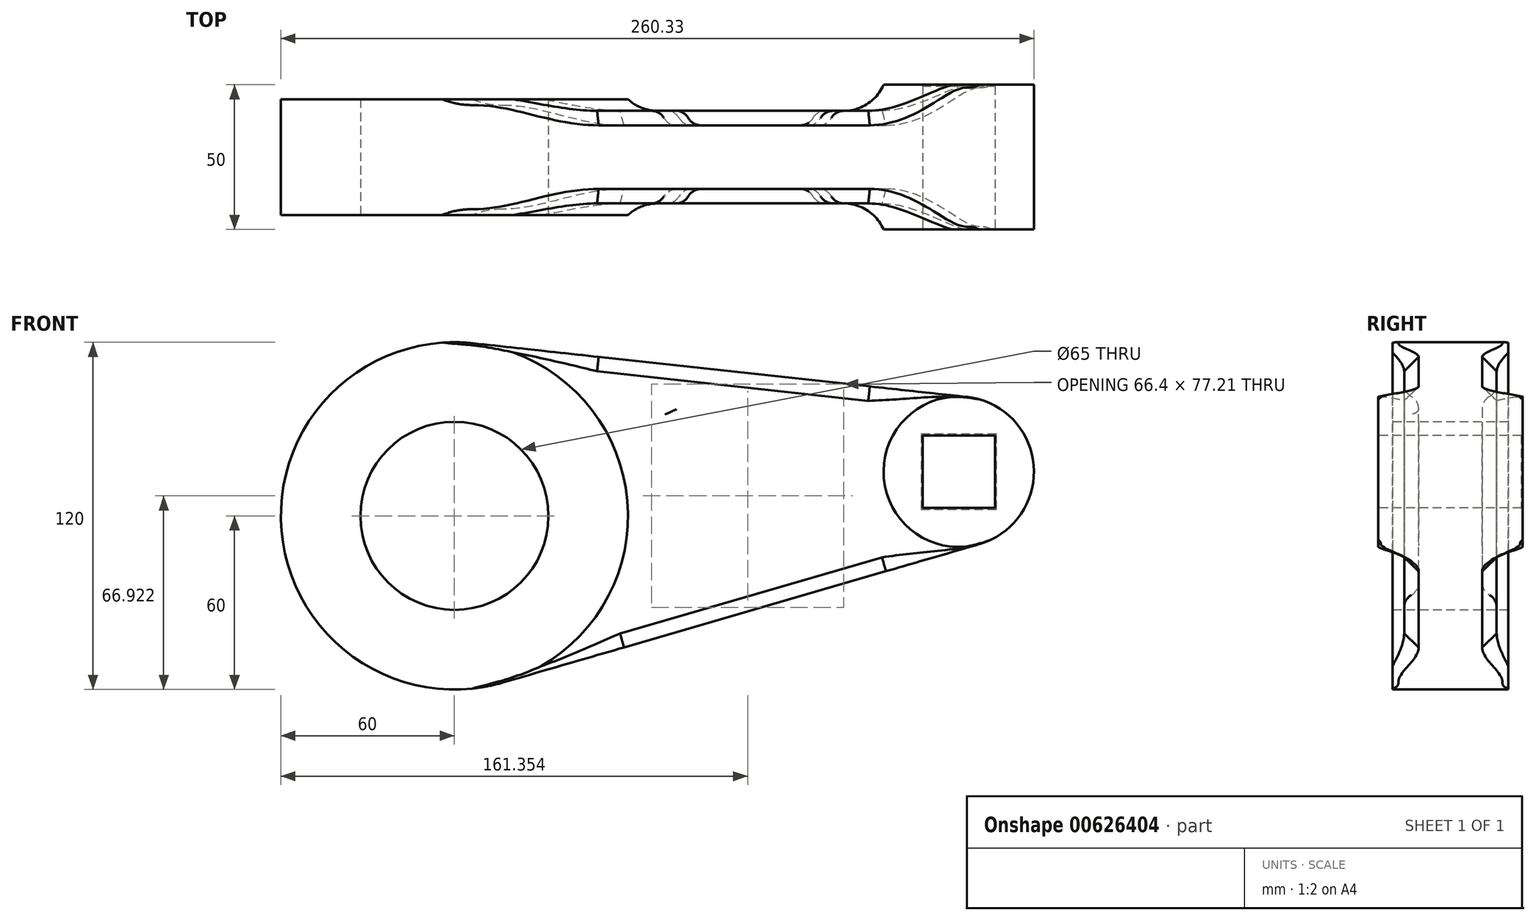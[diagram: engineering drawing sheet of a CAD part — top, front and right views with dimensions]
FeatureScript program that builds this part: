
annotation { "Feature Type Name" : "Feature", "Feature Type Description" : "" }
export const myFeature = defineFeature(function(context is Context, id is Id, definition is map)
    precondition{}
    {
        {
            var Q0;
            Q0=qCreatedBy(makeId("Front.planeOp"),FACE);
            var sketch = newSketch(context, id + "F0", { "sketchPlane" : qUnion([Q0])});
            skCircle(sketch, "E0", {"center": v(0, 0) * mm, "radius": 60 * mm});
            skLineSegment(sketch, "E1", {"start": v(6.48, 59.65) * mm, "end": v(177.14, 41.1) * mm});
            skLineSegment(sketch, "E2", {"start": v(16.74, -57.62) * mm, "end": v(181.59, -9.72) * mm});
            skCircle(sketch, "E3", {"center": v(174.33, 15.25) * mm, "radius": 26 * mm});
            skLineSegment(sketch, "E4", {"start": v(0, 0) * mm, "end": v(174.33, 15.25) * mm});
            skSolve(sketch);
        }
        {
            var Q0;
            {var subQ0=sQuery(id+"F0.wireOp",EDGE,"E0");var subQ1=makeQuery(id+"F0.imprint","INTERSECT",VERTEX,{"derivedFrom":[subQ0,sQuery(id+"F0.wireOp",EDGE,"E1")]});Q0=makeQuery(id+"F0.imprint","IMPRINT",FACE,{"disambiguationData":[TD([[makeQuery(id+"F0.imprint","IMPRINT",EDGE,{"disambiguationData":[TD([[subQ1,1.0]])],"derivedFrom":subQ0}),1.0]])]});}
            var Q1;
            {var subQ0=sQuery(id+"F0.wireOp",EDGE,"E1");Q1=makeQuery(id+"F0.imprint","IMPRINT",FACE,{"disambiguationData":[TD([[makeQuery(id+"F0.imprint","IMPRINT",EDGE,{"derivedFrom":subQ0}),-1.0]])]});}
            var Q2;
            {var subQ0=sQuery(id+"F0.wireOp",EDGE,"E2");Q2=makeQuery(id+"F0.imprint","IMPRINT",FACE,{"disambiguationData":[TD([[makeQuery(id+"F0.imprint","IMPRINT",EDGE,{"derivedFrom":subQ0}),1.0]])]});}
            var Q3;
            {var subQ0=sQuery(id+"F0.wireOp",EDGE,"E3");var subQ1=makeQuery(id+"F0.imprint","INTERSECT",VERTEX,{"derivedFrom":[sQuery(id+"F0.wireOp",EDGE,"E1"),subQ0]});Q3=makeQuery(id+"F0.imprint","IMPRINT",FACE,{"disambiguationData":[TD([[makeQuery(id+"F0.imprint","IMPRINT",EDGE,{"disambiguationData":[TD([[subQ1,-1.0]])],"derivedFrom":subQ0}),1.0]])]});}
            extrude(context, id + "F1", {"entities" : qUnion([Q0, Q1, Q2, Q3]), "endBound" : BoundingType.SYMMETRIC, "depth" : 32 * mm, "offsetDistance" : 25 * mm});
        }
        {
            var Q0;
            {var subQ0=sQuery(id+"F0.wireOp",EDGE,"E0");var subQ1=makeQuery(id+"F0.imprint","INTERSECT",VERTEX,{"derivedFrom":[subQ0,sQuery(id+"F0.wireOp",EDGE,"E1")]});Q0=makeQuery(id+"F0.imprint","IMPRINT",FACE,{"disambiguationData":[TD([[makeQuery(id+"F0.imprint","IMPRINT",EDGE,{"disambiguationData":[TD([[subQ1,1.0]])],"derivedFrom":subQ0}),1.0]])]});}
            extrude(context, id + "F2", {"entities" : qUnion([Q0]), "operationType" : NewBodyOperationType.ADD, "endBound" : BoundingType.SYMMETRIC, "depth" : 40 * mm, "offsetDistance" : 25 * mm});
        }
        {
            var Q0;
            {var subQ0=sQuery(id+"F0.wireOp",EDGE,"E3");var subQ1=makeQuery(id+"F0.imprint","INTERSECT",VERTEX,{"derivedFrom":[sQuery(id+"F0.wireOp",EDGE,"E1"),subQ0]});Q0=makeQuery(id+"F0.imprint","IMPRINT",FACE,{"disambiguationData":[TD([[makeQuery(id+"F0.imprint","IMPRINT",EDGE,{"disambiguationData":[TD([[subQ1,-1.0]])],"derivedFrom":subQ0}),1.0]])]});}
            extrude(context, id + "F3", {"entities" : qUnion([Q0]), "operationType" : NewBodyOperationType.ADD, "endBound" : BoundingType.SYMMETRIC, "depth" : 50 * mm, "offsetDistance" : 25 * mm});
        }
        {
            var Q0;
            Q0=makeQuery(id+"F2.opExtrude","CAP_FACE",FACE,{"disambiguationData":[OSD([sQuery(id+"F0.wireOp",EDGE,"E0")])],"isStart":false});
            var sketch = newSketch(context, id + "F4", { "sketchPlane" : qUnion([Q0])});
            skCircle(sketch, "E5", {"center": v(0, 0) * mm, "radius": 32.5 * mm});
            skSolve(sketch);
        }
        {
            var Q0;
            Q0=makeQuery(id+"F4.imprint","IMPRINT",FACE,{"disambiguationData":[TD([[makeQuery(id+"F4.imprint","IMPRINT",EDGE,{"derivedFrom":sQuery(id+"F4.wireOp",EDGE,"E5")}),1.0]])]});
            extrude(context, id + "F5", {"entities" : qUnion([Q0]), "operationType" : NewBodyOperationType.REMOVE, "endBound" : BoundingType.THROUGH_ALL, "oppositeDirection" : true, "depth" : 25 * mm, "offsetDistance" : 25 * mm});
        }
        {
            var Q0;
            {var subQ0=sQuery(id+"F0.wireOp",EDGE,"E0");Q0=makeQuery(id+"F2.boolean.opBoolean","INTERSECT",EDGE,{"derivedFrom":[makeQuery(id+"F1.opExtrude","CAP_FACE",FACE,{"disambiguationData":[OSD([subQ0,sQuery(id+"F0.wireOp",EDGE,"E1"),sQuery(id+"F0.wireOp",EDGE,"E2"),sQuery(id+"F0.wireOp",EDGE,"E3")])],"isStart":false}),makeQuery(id+"F2.opExtrude","SWEPT_FACE",FACE,{"disambiguationData":[OSD([subQ0])]})]});}
            var Q1;
            {var subQ0=sQuery(id+"F0.wireOp",EDGE,"E0");Q1=makeQuery(id+"F2.boolean.opBoolean","INTERSECT",EDGE,{"derivedFrom":[makeQuery(id+"F1.opExtrude","CAP_FACE",FACE,{"disambiguationData":[OSD([subQ0,sQuery(id+"F0.wireOp",EDGE,"E1"),sQuery(id+"F0.wireOp",EDGE,"E2"),sQuery(id+"F0.wireOp",EDGE,"E3")])],"isStart":true}),makeQuery(id+"F2.opExtrude","SWEPT_FACE",FACE,{"disambiguationData":[OSD([subQ0])]})]});}
            var Q2;
            {var subQ0=sQuery(id+"F0.wireOp",EDGE,"E3");Q2=makeQuery(id+"F3.boolean.opBoolean","INTERSECT",EDGE,{"derivedFrom":[makeQuery(id+"F1.opExtrude","CAP_FACE",FACE,{"disambiguationData":[OSD([sQuery(id+"F0.wireOp",EDGE,"E0"),sQuery(id+"F0.wireOp",EDGE,"E1"),sQuery(id+"F0.wireOp",EDGE,"E2"),subQ0])],"isStart":true}),makeQuery(id+"F3.opExtrude","SWEPT_FACE",FACE,{"disambiguationData":[OSD([subQ0])]})]});}
            var Q3;
            {var subQ0=sQuery(id+"F0.wireOp",EDGE,"E3");Q3=makeQuery(id+"F3.boolean.opBoolean","INTERSECT",EDGE,{"derivedFrom":[makeQuery(id+"F1.opExtrude","CAP_FACE",FACE,{"disambiguationData":[OSD([sQuery(id+"F0.wireOp",EDGE,"E0"),sQuery(id+"F0.wireOp",EDGE,"E1"),sQuery(id+"F0.wireOp",EDGE,"E2"),subQ0])],"isStart":false}),makeQuery(id+"F3.opExtrude","SWEPT_FACE",FACE,{"disambiguationData":[OSD([subQ0])]})]});}
            fillet(context, id + "F6", {"entities" : qUnion([Q0, Q1, Q2, Q3]), "radius" : 15 * mm, "tangentPropagation" : true, "allowEdgeOverflow" : false});
        }
        {
            var Q0;
            Q0=makeQuery(id+"F1.opExtrude","CAP_FACE",FACE,{"disambiguationData":[OSD([sQuery(id+"F0.wireOp",EDGE,"E0"),sQuery(id+"F0.wireOp",EDGE,"E1"),sQuery(id+"F0.wireOp",EDGE,"E2"),sQuery(id+"F0.wireOp",EDGE,"E3")])],"isStart":false});
            var sketch = newSketch(context, id + "F7", { "sketchPlane" : qUnion([Q0])});
            skLineSegment(sketch, "E6.0", {"start": v(74.16, -30.52) * mm, "end": v(133.57, -13.26) * mm});
            skArc(sketch, "E6.1", {"start": v(67.74, 42.93) * mm, "mid": v(79.9, 6.99) * mm, "end": v(74.16, -30.52) * mm});
            skLineSegment(sketch, "E6.2", {"start": v(129.23, 36.25) * mm, "end": v(67.74, 42.93) * mm});
            skArc(sketch, "E6.3", {"start": v(133.57, -13.26) * mm, "mid": v(124.78, 10.92) * mm, "end": v(129.23, 36.25) * mm});
            skSolve(sketch);
        }
        {
            var Q0;
            Q0=makeQuery(id+"F7.imprint","IMPRINT",FACE,{"disambiguationData":[TD([[makeQuery(id+"F7.imprint","IMPRINT",EDGE,{"derivedFrom":sQuery(id+"F7.wireOp",EDGE,"E6.0")}),1.0]])]});
            extrude(context, id + "F8", {"entities" : qUnion([Q0]), "operationType" : NewBodyOperationType.REMOVE, "oppositeDirection" : true, "depth" : 5 * mm, "offsetDistance" : 25 * mm});
        }
        {
            var Q0;
            Q0=makeQuery(id+"F1.opExtrude","CAP_FACE",FACE,{"disambiguationData":[OSD([sQuery(id+"F0.wireOp",EDGE,"E0"),sQuery(id+"F0.wireOp",EDGE,"E1"),sQuery(id+"F0.wireOp",EDGE,"E2"),sQuery(id+"F0.wireOp",EDGE,"E3")])],"isStart":true});
            var sketch = newSketch(context, id + "F9", { "sketchPlane" : qUnion([Q0])});
            skLineSegment(sketch, "E7.0", {"start": v(-67.74, 42.93) * mm, "end": v(-129.23, 36.25) * mm});
            skArc(sketch, "E7.1", {"start": v(-74.16, -30.52) * mm, "mid": v(-79.9, 6.99) * mm, "end": v(-67.74, 42.93) * mm});
            skLineSegment(sketch, "E7.2", {"start": v(-133.57, -13.26) * mm, "end": v(-74.16, -30.52) * mm});
            skArc(sketch, "E7.3", {"start": v(-129.23, 36.25) * mm, "mid": v(-124.78, 10.92) * mm, "end": v(-133.57, -13.26) * mm});
            skSolve(sketch);
        }
        {
            var Q0;
            Q0=makeQuery(id+"F9.imprint","IMPRINT",FACE,{"disambiguationData":[TD([[makeQuery(id+"F9.imprint","IMPRINT",EDGE,{"derivedFrom":sQuery(id+"F9.wireOp",EDGE,"E7.0")}),1.0]])]});
            extrude(context, id + "F10", {"entities" : qUnion([Q0]), "operationType" : NewBodyOperationType.REMOVE, "oppositeDirection" : true, "depth" : 5 * mm, "offsetDistance" : 25 * mm});
        }
        {
            var Q0;
            Q0=makeQuery(id+"F8.boolean.opBoolean","COPY",EDGE,{"derivedFrom":makeQuery(id+"F8.opExtrude","SWEPT_EDGE",EDGE,{"disambiguationData":[OSD([sQuery(id+"F7.wireOp",EDGE,"E6.0"),sQuery(id+"F7.wireOp",EDGE,"E6.1")])]})});
            var Q1;
            Q1=makeQuery(id+"F8.boolean.opBoolean","COPY",EDGE,{"derivedFrom":makeQuery(id+"F8.opExtrude","SWEPT_EDGE",EDGE,{"disambiguationData":[OSD([sQuery(id+"F7.wireOp",EDGE,"E6.1"),sQuery(id+"F7.wireOp",EDGE,"E6.2")])]})});
            var Q2;
            Q2=makeQuery(id+"F8.boolean.opBoolean","COPY",EDGE,{"derivedFrom":makeQuery(id+"F8.opExtrude","SWEPT_EDGE",EDGE,{"disambiguationData":[OSD([sQuery(id+"F7.wireOp",EDGE,"E6.2"),sQuery(id+"F7.wireOp",EDGE,"E6.3")])]})});
            var Q3;
            Q3=makeQuery(id+"F8.boolean.opBoolean","COPY",EDGE,{"derivedFrom":makeQuery(id+"F8.opExtrude","SWEPT_EDGE",EDGE,{"disambiguationData":[OSD([sQuery(id+"F7.wireOp",EDGE,"E6.0"),sQuery(id+"F7.wireOp",EDGE,"E6.3")])]})});
            fillet(context, id + "F11", {"entities" : qUnion([Q0, Q1, Q2, Q3]), "radius" : 5 * mm, "tangentPropagation" : true, "allowEdgeOverflow" : false});
        }
        {
            var Q0;
            Q0=makeQuery(id+"F10.boolean.opBoolean","COPY",EDGE,{"derivedFrom":makeQuery(id+"F10.opExtrude","SWEPT_EDGE",EDGE,{"disambiguationData":[OSD([sQuery(id+"F9.wireOp",EDGE,"E7.2"),sQuery(id+"F9.wireOp",EDGE,"E7.3")])]})});
            var Q1;
            Q1=makeQuery(id+"F10.boolean.opBoolean","COPY",EDGE,{"derivedFrom":makeQuery(id+"F10.opExtrude","SWEPT_EDGE",EDGE,{"disambiguationData":[OSD([sQuery(id+"F9.wireOp",EDGE,"E7.0"),sQuery(id+"F9.wireOp",EDGE,"E7.3")])]})});
            var Q2;
            Q2=makeQuery(id+"F10.boolean.opBoolean","COPY",EDGE,{"derivedFrom":makeQuery(id+"F10.opExtrude","SWEPT_EDGE",EDGE,{"disambiguationData":[OSD([sQuery(id+"F9.wireOp",EDGE,"E7.0"),sQuery(id+"F9.wireOp",EDGE,"E7.1")])]})});
            var Q3;
            Q3=makeQuery(id+"F10.boolean.opBoolean","COPY",EDGE,{"derivedFrom":makeQuery(id+"F10.opExtrude","SWEPT_EDGE",EDGE,{"disambiguationData":[OSD([sQuery(id+"F9.wireOp",EDGE,"E7.1"),sQuery(id+"F9.wireOp",EDGE,"E7.2")])]})});
            fillet(context, id + "F12", {"entities" : qUnion([Q0, Q1, Q2, Q3]), "radius" : 5 * mm, "tangentPropagation" : true, "allowEdgeOverflow" : false});
        }
        {
            var Q0;
            Q0=makeQuery(id+"F10.boolean.opBoolean","COPY",FACE,{"derivedFrom":makeQuery(id+"F10.opExtrude","CAP_FACE",FACE,{"disambiguationData":[OSD([sQuery(id+"F9.wireOp",EDGE,"E7.0"),sQuery(id+"F9.wireOp",EDGE,"E7.1"),sQuery(id+"F9.wireOp",EDGE,"E7.2"),sQuery(id+"F9.wireOp",EDGE,"E7.3")])],"isStart":false})});
            fillet(context, id + "F13", {"entities" : qUnion([Q0]), "radius" : 5 * mm, "tangentPropagation" : true, "allowEdgeOverflow" : false});
        }
        {
            var Q0;
            Q0=makeQuery(id+"F8.boolean.opBoolean","COPY",FACE,{"derivedFrom":makeQuery(id+"F8.opExtrude","CAP_FACE",FACE,{"disambiguationData":[OSD([sQuery(id+"F7.wireOp",EDGE,"E6.0"),sQuery(id+"F7.wireOp",EDGE,"E6.1"),sQuery(id+"F7.wireOp",EDGE,"E6.2"),sQuery(id+"F7.wireOp",EDGE,"E6.3")])],"isStart":false})});
            fillet(context, id + "F14", {"entities" : qUnion([Q0]), "radius" : 5 * mm, "tangentPropagation" : true, "allowEdgeOverflow" : false});
        }
        {
            var Q0;
            Q0=makeQuery(id+"F14.opFillet","BLEND_EDGE",EDGE,{"blendedFrom":[makeQuery(id+"F8.boolean.opBoolean","COPY",EDGE,{"derivedFrom":makeQuery(id+"F8.opExtrude","CAP_EDGE",EDGE,{"disambiguationData":[OSD([sQuery(id+"F7.wireOp",EDGE,"E6.2")])],"isStart":false})}),makeQuery(id+"F1.opExtrude","CAP_FACE",FACE,{"disambiguationData":[OSD([sQuery(id+"F0.wireOp",EDGE,"E0"),sQuery(id+"F0.wireOp",EDGE,"E1"),sQuery(id+"F0.wireOp",EDGE,"E2"),sQuery(id+"F0.wireOp",EDGE,"E3")])],"isStart":false})],"blendedInto":[makeQuery(id+"F1.opExtrude","CAP_FACE",FACE,{"disambiguationData":[OSD([sQuery(id+"F0.wireOp",EDGE,"E0"),sQuery(id+"F0.wireOp",EDGE,"E1"),sQuery(id+"F0.wireOp",EDGE,"E2"),sQuery(id+"F0.wireOp",EDGE,"E3")])],"isStart":false})]});
            var Q1;
            {var subQ0=sQuery(id+"F7.wireOp",EDGE,"E6.2");var subQ1=sQuery(id+"F7.wireOp",EDGE,"E6.1");Q1=makeQuery(id+"F14.opFillet","BLEND_EDGE",EDGE,{"blendedFrom":[makeQuery(id+"F11.opFillet","BLEND_EDGE",EDGE,{"blendedFrom":[makeQuery(id+"F8.boolean.opBoolean","COPY",EDGE,{"derivedFrom":makeQuery(id+"F8.opExtrude","SWEPT_EDGE",EDGE,{"disambiguationData":[OSD([subQ1,subQ0])]})}),makeQuery(id+"F8.boolean.opBoolean","COPY",FACE,{"derivedFrom":makeQuery(id+"F8.opExtrude","CAP_FACE",FACE,{"disambiguationData":[OSD([sQuery(id+"F7.wireOp",EDGE,"E6.0"),subQ1,subQ0,sQuery(id+"F7.wireOp",EDGE,"E6.3")])],"isStart":false})})],"blendedInto":[makeQuery(id+"F8.boolean.opBoolean","COPY",FACE,{"derivedFrom":makeQuery(id+"F8.opExtrude","CAP_FACE",FACE,{"disambiguationData":[OSD([sQuery(id+"F7.wireOp",EDGE,"E6.0"),subQ1,subQ0,sQuery(id+"F7.wireOp",EDGE,"E6.3")])],"isStart":false})})]}),makeQuery(id+"F1.opExtrude","CAP_FACE",FACE,{"disambiguationData":[OSD([sQuery(id+"F0.wireOp",EDGE,"E0"),sQuery(id+"F0.wireOp",EDGE,"E1"),sQuery(id+"F0.wireOp",EDGE,"E2"),sQuery(id+"F0.wireOp",EDGE,"E3")])],"isStart":false})],"blendedInto":[makeQuery(id+"F1.opExtrude","CAP_FACE",FACE,{"disambiguationData":[OSD([sQuery(id+"F0.wireOp",EDGE,"E0"),sQuery(id+"F0.wireOp",EDGE,"E1"),sQuery(id+"F0.wireOp",EDGE,"E2"),sQuery(id+"F0.wireOp",EDGE,"E3")])],"isStart":false})]});}
            var Q2;
            Q2=makeQuery(id+"F14.opFillet","BLEND_EDGE",EDGE,{"blendedFrom":[makeQuery(id+"F8.boolean.opBoolean","COPY",EDGE,{"derivedFrom":makeQuery(id+"F8.opExtrude","CAP_EDGE",EDGE,{"disambiguationData":[OSD([sQuery(id+"F7.wireOp",EDGE,"E6.1")])],"isStart":false})}),makeQuery(id+"F1.opExtrude","CAP_FACE",FACE,{"disambiguationData":[OSD([sQuery(id+"F0.wireOp",EDGE,"E0"),sQuery(id+"F0.wireOp",EDGE,"E1"),sQuery(id+"F0.wireOp",EDGE,"E2"),sQuery(id+"F0.wireOp",EDGE,"E3")])],"isStart":false})],"blendedInto":[makeQuery(id+"F1.opExtrude","CAP_FACE",FACE,{"disambiguationData":[OSD([sQuery(id+"F0.wireOp",EDGE,"E0"),sQuery(id+"F0.wireOp",EDGE,"E1"),sQuery(id+"F0.wireOp",EDGE,"E2"),sQuery(id+"F0.wireOp",EDGE,"E3")])],"isStart":false})]});
            var Q3;
            {var subQ0=sQuery(id+"F7.wireOp",EDGE,"E6.1");var subQ1=sQuery(id+"F7.wireOp",EDGE,"E6.0");Q3=makeQuery(id+"F14.opFillet","BLEND_EDGE",EDGE,{"blendedFrom":[makeQuery(id+"F11.opFillet","BLEND_EDGE",EDGE,{"blendedFrom":[makeQuery(id+"F8.boolean.opBoolean","COPY",EDGE,{"derivedFrom":makeQuery(id+"F8.opExtrude","SWEPT_EDGE",EDGE,{"disambiguationData":[OSD([subQ1,subQ0])]})}),makeQuery(id+"F8.boolean.opBoolean","COPY",FACE,{"derivedFrom":makeQuery(id+"F8.opExtrude","CAP_FACE",FACE,{"disambiguationData":[OSD([subQ1,subQ0,sQuery(id+"F7.wireOp",EDGE,"E6.2"),sQuery(id+"F7.wireOp",EDGE,"E6.3")])],"isStart":false})})],"blendedInto":[makeQuery(id+"F8.boolean.opBoolean","COPY",FACE,{"derivedFrom":makeQuery(id+"F8.opExtrude","CAP_FACE",FACE,{"disambiguationData":[OSD([subQ1,subQ0,sQuery(id+"F7.wireOp",EDGE,"E6.2"),sQuery(id+"F7.wireOp",EDGE,"E6.3")])],"isStart":false})})]}),makeQuery(id+"F1.opExtrude","CAP_FACE",FACE,{"disambiguationData":[OSD([sQuery(id+"F0.wireOp",EDGE,"E0"),sQuery(id+"F0.wireOp",EDGE,"E1"),sQuery(id+"F0.wireOp",EDGE,"E2"),sQuery(id+"F0.wireOp",EDGE,"E3")])],"isStart":false})],"blendedInto":[makeQuery(id+"F1.opExtrude","CAP_FACE",FACE,{"disambiguationData":[OSD([sQuery(id+"F0.wireOp",EDGE,"E0"),sQuery(id+"F0.wireOp",EDGE,"E1"),sQuery(id+"F0.wireOp",EDGE,"E2"),sQuery(id+"F0.wireOp",EDGE,"E3")])],"isStart":false})]});}
            var Q4;
            Q4=makeQuery(id+"F14.opFillet","BLEND_EDGE",EDGE,{"blendedFrom":[makeQuery(id+"F8.boolean.opBoolean","COPY",EDGE,{"derivedFrom":makeQuery(id+"F8.opExtrude","CAP_EDGE",EDGE,{"disambiguationData":[OSD([sQuery(id+"F7.wireOp",EDGE,"E6.0")])],"isStart":false})}),makeQuery(id+"F1.opExtrude","CAP_FACE",FACE,{"disambiguationData":[OSD([sQuery(id+"F0.wireOp",EDGE,"E0"),sQuery(id+"F0.wireOp",EDGE,"E1"),sQuery(id+"F0.wireOp",EDGE,"E2"),sQuery(id+"F0.wireOp",EDGE,"E3")])],"isStart":false})],"blendedInto":[makeQuery(id+"F1.opExtrude","CAP_FACE",FACE,{"disambiguationData":[OSD([sQuery(id+"F0.wireOp",EDGE,"E0"),sQuery(id+"F0.wireOp",EDGE,"E1"),sQuery(id+"F0.wireOp",EDGE,"E2"),sQuery(id+"F0.wireOp",EDGE,"E3")])],"isStart":false})]});
            var Q5;
            {var subQ0=sQuery(id+"F7.wireOp",EDGE,"E6.3");var subQ1=sQuery(id+"F7.wireOp",EDGE,"E6.0");Q5=makeQuery(id+"F14.opFillet","BLEND_EDGE",EDGE,{"blendedFrom":[makeQuery(id+"F11.opFillet","BLEND_EDGE",EDGE,{"blendedFrom":[makeQuery(id+"F8.boolean.opBoolean","COPY",EDGE,{"derivedFrom":makeQuery(id+"F8.opExtrude","SWEPT_EDGE",EDGE,{"disambiguationData":[OSD([subQ1,subQ0])]})}),makeQuery(id+"F8.boolean.opBoolean","COPY",FACE,{"derivedFrom":makeQuery(id+"F8.opExtrude","CAP_FACE",FACE,{"disambiguationData":[OSD([subQ1,sQuery(id+"F7.wireOp",EDGE,"E6.1"),sQuery(id+"F7.wireOp",EDGE,"E6.2"),subQ0])],"isStart":false})})],"blendedInto":[makeQuery(id+"F8.boolean.opBoolean","COPY",FACE,{"derivedFrom":makeQuery(id+"F8.opExtrude","CAP_FACE",FACE,{"disambiguationData":[OSD([subQ1,sQuery(id+"F7.wireOp",EDGE,"E6.1"),sQuery(id+"F7.wireOp",EDGE,"E6.2"),subQ0])],"isStart":false})})]}),makeQuery(id+"F1.opExtrude","CAP_FACE",FACE,{"disambiguationData":[OSD([sQuery(id+"F0.wireOp",EDGE,"E0"),sQuery(id+"F0.wireOp",EDGE,"E1"),sQuery(id+"F0.wireOp",EDGE,"E2"),sQuery(id+"F0.wireOp",EDGE,"E3")])],"isStart":false})],"blendedInto":[makeQuery(id+"F1.opExtrude","CAP_FACE",FACE,{"disambiguationData":[OSD([sQuery(id+"F0.wireOp",EDGE,"E0"),sQuery(id+"F0.wireOp",EDGE,"E1"),sQuery(id+"F0.wireOp",EDGE,"E2"),sQuery(id+"F0.wireOp",EDGE,"E3")])],"isStart":false})]});}
            var Q6;
            Q6=makeQuery(id+"F14.opFillet","BLEND_EDGE",EDGE,{"blendedFrom":[makeQuery(id+"F8.boolean.opBoolean","COPY",EDGE,{"derivedFrom":makeQuery(id+"F8.opExtrude","CAP_EDGE",EDGE,{"disambiguationData":[OSD([sQuery(id+"F7.wireOp",EDGE,"E6.3")])],"isStart":false})}),makeQuery(id+"F1.opExtrude","CAP_FACE",FACE,{"disambiguationData":[OSD([sQuery(id+"F0.wireOp",EDGE,"E0"),sQuery(id+"F0.wireOp",EDGE,"E1"),sQuery(id+"F0.wireOp",EDGE,"E2"),sQuery(id+"F0.wireOp",EDGE,"E3")])],"isStart":false})],"blendedInto":[makeQuery(id+"F1.opExtrude","CAP_FACE",FACE,{"disambiguationData":[OSD([sQuery(id+"F0.wireOp",EDGE,"E0"),sQuery(id+"F0.wireOp",EDGE,"E1"),sQuery(id+"F0.wireOp",EDGE,"E2"),sQuery(id+"F0.wireOp",EDGE,"E3")])],"isStart":false})]});
            var Q7;
            {var subQ0=sQuery(id+"F7.wireOp",EDGE,"E6.3");var subQ1=sQuery(id+"F7.wireOp",EDGE,"E6.2");Q7=makeQuery(id+"F14.opFillet","BLEND_EDGE",EDGE,{"blendedFrom":[makeQuery(id+"F11.opFillet","BLEND_EDGE",EDGE,{"blendedFrom":[makeQuery(id+"F8.boolean.opBoolean","COPY",EDGE,{"derivedFrom":makeQuery(id+"F8.opExtrude","SWEPT_EDGE",EDGE,{"disambiguationData":[OSD([subQ1,subQ0])]})}),makeQuery(id+"F8.boolean.opBoolean","COPY",FACE,{"derivedFrom":makeQuery(id+"F8.opExtrude","CAP_FACE",FACE,{"disambiguationData":[OSD([sQuery(id+"F7.wireOp",EDGE,"E6.0"),sQuery(id+"F7.wireOp",EDGE,"E6.1"),subQ1,subQ0])],"isStart":false})})],"blendedInto":[makeQuery(id+"F8.boolean.opBoolean","COPY",FACE,{"derivedFrom":makeQuery(id+"F8.opExtrude","CAP_FACE",FACE,{"disambiguationData":[OSD([sQuery(id+"F7.wireOp",EDGE,"E6.0"),sQuery(id+"F7.wireOp",EDGE,"E6.1"),subQ1,subQ0])],"isStart":false})})]}),makeQuery(id+"F1.opExtrude","CAP_FACE",FACE,{"disambiguationData":[OSD([sQuery(id+"F0.wireOp",EDGE,"E0"),sQuery(id+"F0.wireOp",EDGE,"E1"),sQuery(id+"F0.wireOp",EDGE,"E2"),sQuery(id+"F0.wireOp",EDGE,"E3")])],"isStart":false})],"blendedInto":[makeQuery(id+"F1.opExtrude","CAP_FACE",FACE,{"disambiguationData":[OSD([sQuery(id+"F0.wireOp",EDGE,"E0"),sQuery(id+"F0.wireOp",EDGE,"E1"),sQuery(id+"F0.wireOp",EDGE,"E2"),sQuery(id+"F0.wireOp",EDGE,"E3")])],"isStart":false})]});}
            fillet(context, id + "F15", {"entities" : qUnion([Q0, Q1, Q2, Q3, Q4, Q5, Q6, Q7]), "radius" : 5 * mm, "tangentPropagation" : true, "allowEdgeOverflow" : false});
        }
        {
            var Q0;
            Q0=makeQuery(id+"F13.opFillet","BLEND_EDGE",EDGE,{"blendedFrom":[makeQuery(id+"F10.boolean.opBoolean","COPY",EDGE,{"derivedFrom":makeQuery(id+"F10.opExtrude","CAP_EDGE",EDGE,{"disambiguationData":[OSD([sQuery(id+"F9.wireOp",EDGE,"E7.0")])],"isStart":false})}),makeQuery(id+"F1.opExtrude","CAP_FACE",FACE,{"disambiguationData":[OSD([sQuery(id+"F0.wireOp",EDGE,"E0"),sQuery(id+"F0.wireOp",EDGE,"E1"),sQuery(id+"F0.wireOp",EDGE,"E2"),sQuery(id+"F0.wireOp",EDGE,"E3")])],"isStart":true})],"blendedInto":[makeQuery(id+"F1.opExtrude","CAP_FACE",FACE,{"disambiguationData":[OSD([sQuery(id+"F0.wireOp",EDGE,"E0"),sQuery(id+"F0.wireOp",EDGE,"E1"),sQuery(id+"F0.wireOp",EDGE,"E2"),sQuery(id+"F0.wireOp",EDGE,"E3")])],"isStart":true})]});
            var Q1;
            {var subQ0=sQuery(id+"F9.wireOp",EDGE,"E7.1");var subQ1=sQuery(id+"F9.wireOp",EDGE,"E7.0");Q1=makeQuery(id+"F13.opFillet","BLEND_EDGE",EDGE,{"blendedFrom":[makeQuery(id+"F12.opFillet","BLEND_EDGE",EDGE,{"blendedFrom":[makeQuery(id+"F10.boolean.opBoolean","COPY",EDGE,{"derivedFrom":makeQuery(id+"F10.opExtrude","SWEPT_EDGE",EDGE,{"disambiguationData":[OSD([subQ1,subQ0])]})}),makeQuery(id+"F10.boolean.opBoolean","COPY",FACE,{"derivedFrom":makeQuery(id+"F10.opExtrude","CAP_FACE",FACE,{"disambiguationData":[OSD([subQ1,subQ0,sQuery(id+"F9.wireOp",EDGE,"E7.2"),sQuery(id+"F9.wireOp",EDGE,"E7.3")])],"isStart":false})})],"blendedInto":[makeQuery(id+"F10.boolean.opBoolean","COPY",FACE,{"derivedFrom":makeQuery(id+"F10.opExtrude","CAP_FACE",FACE,{"disambiguationData":[OSD([subQ1,subQ0,sQuery(id+"F9.wireOp",EDGE,"E7.2"),sQuery(id+"F9.wireOp",EDGE,"E7.3")])],"isStart":false})})]}),makeQuery(id+"F1.opExtrude","CAP_FACE",FACE,{"disambiguationData":[OSD([sQuery(id+"F0.wireOp",EDGE,"E0"),sQuery(id+"F0.wireOp",EDGE,"E1"),sQuery(id+"F0.wireOp",EDGE,"E2"),sQuery(id+"F0.wireOp",EDGE,"E3")])],"isStart":true})],"blendedInto":[makeQuery(id+"F1.opExtrude","CAP_FACE",FACE,{"disambiguationData":[OSD([sQuery(id+"F0.wireOp",EDGE,"E0"),sQuery(id+"F0.wireOp",EDGE,"E1"),sQuery(id+"F0.wireOp",EDGE,"E2"),sQuery(id+"F0.wireOp",EDGE,"E3")])],"isStart":true})]});}
            var Q2;
            Q2=makeQuery(id+"F13.opFillet","BLEND_EDGE",EDGE,{"blendedFrom":[makeQuery(id+"F10.boolean.opBoolean","COPY",EDGE,{"derivedFrom":makeQuery(id+"F10.opExtrude","CAP_EDGE",EDGE,{"disambiguationData":[OSD([sQuery(id+"F9.wireOp",EDGE,"E7.1")])],"isStart":false})}),makeQuery(id+"F1.opExtrude","CAP_FACE",FACE,{"disambiguationData":[OSD([sQuery(id+"F0.wireOp",EDGE,"E0"),sQuery(id+"F0.wireOp",EDGE,"E1"),sQuery(id+"F0.wireOp",EDGE,"E2"),sQuery(id+"F0.wireOp",EDGE,"E3")])],"isStart":true})],"blendedInto":[makeQuery(id+"F1.opExtrude","CAP_FACE",FACE,{"disambiguationData":[OSD([sQuery(id+"F0.wireOp",EDGE,"E0"),sQuery(id+"F0.wireOp",EDGE,"E1"),sQuery(id+"F0.wireOp",EDGE,"E2"),sQuery(id+"F0.wireOp",EDGE,"E3")])],"isStart":true})]});
            var Q3;
            {var subQ0=sQuery(id+"F9.wireOp",EDGE,"E7.2");var subQ1=sQuery(id+"F9.wireOp",EDGE,"E7.1");Q3=makeQuery(id+"F13.opFillet","BLEND_EDGE",EDGE,{"blendedFrom":[makeQuery(id+"F12.opFillet","BLEND_EDGE",EDGE,{"blendedFrom":[makeQuery(id+"F10.boolean.opBoolean","COPY",EDGE,{"derivedFrom":makeQuery(id+"F10.opExtrude","SWEPT_EDGE",EDGE,{"disambiguationData":[OSD([subQ1,subQ0])]})}),makeQuery(id+"F10.boolean.opBoolean","COPY",FACE,{"derivedFrom":makeQuery(id+"F10.opExtrude","CAP_FACE",FACE,{"disambiguationData":[OSD([sQuery(id+"F9.wireOp",EDGE,"E7.0"),subQ1,subQ0,sQuery(id+"F9.wireOp",EDGE,"E7.3")])],"isStart":false})})],"blendedInto":[makeQuery(id+"F10.boolean.opBoolean","COPY",FACE,{"derivedFrom":makeQuery(id+"F10.opExtrude","CAP_FACE",FACE,{"disambiguationData":[OSD([sQuery(id+"F9.wireOp",EDGE,"E7.0"),subQ1,subQ0,sQuery(id+"F9.wireOp",EDGE,"E7.3")])],"isStart":false})})]}),makeQuery(id+"F1.opExtrude","CAP_FACE",FACE,{"disambiguationData":[OSD([sQuery(id+"F0.wireOp",EDGE,"E0"),sQuery(id+"F0.wireOp",EDGE,"E1"),sQuery(id+"F0.wireOp",EDGE,"E2"),sQuery(id+"F0.wireOp",EDGE,"E3")])],"isStart":true})],"blendedInto":[makeQuery(id+"F1.opExtrude","CAP_FACE",FACE,{"disambiguationData":[OSD([sQuery(id+"F0.wireOp",EDGE,"E0"),sQuery(id+"F0.wireOp",EDGE,"E1"),sQuery(id+"F0.wireOp",EDGE,"E2"),sQuery(id+"F0.wireOp",EDGE,"E3")])],"isStart":true})]});}
            var Q4;
            Q4=makeQuery(id+"F13.opFillet","BLEND_EDGE",EDGE,{"blendedFrom":[makeQuery(id+"F10.boolean.opBoolean","COPY",EDGE,{"derivedFrom":makeQuery(id+"F10.opExtrude","CAP_EDGE",EDGE,{"disambiguationData":[OSD([sQuery(id+"F9.wireOp",EDGE,"E7.2")])],"isStart":false})}),makeQuery(id+"F1.opExtrude","CAP_FACE",FACE,{"disambiguationData":[OSD([sQuery(id+"F0.wireOp",EDGE,"E0"),sQuery(id+"F0.wireOp",EDGE,"E1"),sQuery(id+"F0.wireOp",EDGE,"E2"),sQuery(id+"F0.wireOp",EDGE,"E3")])],"isStart":true})],"blendedInto":[makeQuery(id+"F1.opExtrude","CAP_FACE",FACE,{"disambiguationData":[OSD([sQuery(id+"F0.wireOp",EDGE,"E0"),sQuery(id+"F0.wireOp",EDGE,"E1"),sQuery(id+"F0.wireOp",EDGE,"E2"),sQuery(id+"F0.wireOp",EDGE,"E3")])],"isStart":true})]});
            var Q5;
            {var subQ0=sQuery(id+"F9.wireOp",EDGE,"E7.3");var subQ1=sQuery(id+"F9.wireOp",EDGE,"E7.2");Q5=makeQuery(id+"F13.opFillet","BLEND_EDGE",EDGE,{"blendedFrom":[makeQuery(id+"F12.opFillet","BLEND_EDGE",EDGE,{"blendedFrom":[makeQuery(id+"F10.boolean.opBoolean","COPY",EDGE,{"derivedFrom":makeQuery(id+"F10.opExtrude","SWEPT_EDGE",EDGE,{"disambiguationData":[OSD([subQ1,subQ0])]})}),makeQuery(id+"F10.boolean.opBoolean","COPY",FACE,{"derivedFrom":makeQuery(id+"F10.opExtrude","CAP_FACE",FACE,{"disambiguationData":[OSD([sQuery(id+"F9.wireOp",EDGE,"E7.0"),sQuery(id+"F9.wireOp",EDGE,"E7.1"),subQ1,subQ0])],"isStart":false})})],"blendedInto":[makeQuery(id+"F10.boolean.opBoolean","COPY",FACE,{"derivedFrom":makeQuery(id+"F10.opExtrude","CAP_FACE",FACE,{"disambiguationData":[OSD([sQuery(id+"F9.wireOp",EDGE,"E7.0"),sQuery(id+"F9.wireOp",EDGE,"E7.1"),subQ1,subQ0])],"isStart":false})})]}),makeQuery(id+"F1.opExtrude","CAP_FACE",FACE,{"disambiguationData":[OSD([sQuery(id+"F0.wireOp",EDGE,"E0"),sQuery(id+"F0.wireOp",EDGE,"E1"),sQuery(id+"F0.wireOp",EDGE,"E2"),sQuery(id+"F0.wireOp",EDGE,"E3")])],"isStart":true})],"blendedInto":[makeQuery(id+"F1.opExtrude","CAP_FACE",FACE,{"disambiguationData":[OSD([sQuery(id+"F0.wireOp",EDGE,"E0"),sQuery(id+"F0.wireOp",EDGE,"E1"),sQuery(id+"F0.wireOp",EDGE,"E2"),sQuery(id+"F0.wireOp",EDGE,"E3")])],"isStart":true})]});}
            var Q6;
            Q6=makeQuery(id+"F13.opFillet","BLEND_EDGE",EDGE,{"blendedFrom":[makeQuery(id+"F10.boolean.opBoolean","COPY",EDGE,{"derivedFrom":makeQuery(id+"F10.opExtrude","CAP_EDGE",EDGE,{"disambiguationData":[OSD([sQuery(id+"F9.wireOp",EDGE,"E7.3")])],"isStart":false})}),makeQuery(id+"F1.opExtrude","CAP_FACE",FACE,{"disambiguationData":[OSD([sQuery(id+"F0.wireOp",EDGE,"E0"),sQuery(id+"F0.wireOp",EDGE,"E1"),sQuery(id+"F0.wireOp",EDGE,"E2"),sQuery(id+"F0.wireOp",EDGE,"E3")])],"isStart":true})],"blendedInto":[makeQuery(id+"F1.opExtrude","CAP_FACE",FACE,{"disambiguationData":[OSD([sQuery(id+"F0.wireOp",EDGE,"E0"),sQuery(id+"F0.wireOp",EDGE,"E1"),sQuery(id+"F0.wireOp",EDGE,"E2"),sQuery(id+"F0.wireOp",EDGE,"E3")])],"isStart":true})]});
            var Q7;
            {var subQ0=sQuery(id+"F9.wireOp",EDGE,"E7.3");var subQ1=sQuery(id+"F9.wireOp",EDGE,"E7.0");Q7=makeQuery(id+"F13.opFillet","BLEND_EDGE",EDGE,{"blendedFrom":[makeQuery(id+"F12.opFillet","BLEND_EDGE",EDGE,{"blendedFrom":[makeQuery(id+"F10.boolean.opBoolean","COPY",EDGE,{"derivedFrom":makeQuery(id+"F10.opExtrude","SWEPT_EDGE",EDGE,{"disambiguationData":[OSD([subQ1,subQ0])]})}),makeQuery(id+"F10.boolean.opBoolean","COPY",FACE,{"derivedFrom":makeQuery(id+"F10.opExtrude","CAP_FACE",FACE,{"disambiguationData":[OSD([subQ1,sQuery(id+"F9.wireOp",EDGE,"E7.1"),sQuery(id+"F9.wireOp",EDGE,"E7.2"),subQ0])],"isStart":false})})],"blendedInto":[makeQuery(id+"F10.boolean.opBoolean","COPY",FACE,{"derivedFrom":makeQuery(id+"F10.opExtrude","CAP_FACE",FACE,{"disambiguationData":[OSD([subQ1,sQuery(id+"F9.wireOp",EDGE,"E7.1"),sQuery(id+"F9.wireOp",EDGE,"E7.2"),subQ0])],"isStart":false})})]}),makeQuery(id+"F1.opExtrude","CAP_FACE",FACE,{"disambiguationData":[OSD([sQuery(id+"F0.wireOp",EDGE,"E0"),sQuery(id+"F0.wireOp",EDGE,"E1"),sQuery(id+"F0.wireOp",EDGE,"E2"),sQuery(id+"F0.wireOp",EDGE,"E3")])],"isStart":true})],"blendedInto":[makeQuery(id+"F1.opExtrude","CAP_FACE",FACE,{"disambiguationData":[OSD([sQuery(id+"F0.wireOp",EDGE,"E0"),sQuery(id+"F0.wireOp",EDGE,"E1"),sQuery(id+"F0.wireOp",EDGE,"E2"),sQuery(id+"F0.wireOp",EDGE,"E3")])],"isStart":true})]});}
            fillet(context, id + "F16", {"entities" : qUnion([Q0, Q1, Q2, Q3, Q4, Q5, Q6, Q7]), "radius" : 5 * mm, "tangentPropagation" : true, "allowEdgeOverflow" : false});
        }
        {
            var Q0;
            Q0=makeQuery(id+"F1.opExtrude","CAP_EDGE",EDGE,{"disambiguationData":[OSD([sQuery(id+"F0.wireOp",EDGE,"E1")])],"isStart":true});
            var Q1;
            Q1=makeQuery(id+"F1.opExtrude","CAP_EDGE",EDGE,{"disambiguationData":[OSD([sQuery(id+"F0.wireOp",EDGE,"E2")])],"isStart":true});
            var Q2;
            Q2=makeQuery(id+"F1.opExtrude","CAP_EDGE",EDGE,{"disambiguationData":[OSD([sQuery(id+"F0.wireOp",EDGE,"E1")])],"isStart":false});
            var Q3;
            Q3=makeQuery(id+"F1.opExtrude","CAP_EDGE",EDGE,{"disambiguationData":[OSD([sQuery(id+"F0.wireOp",EDGE,"E2")])],"isStart":false});
            chamfer(context, id + "F17", {"entities" : qUnion([Q0, Q1, Q2, Q3]), "width" : 5 * mm, "tangentPropagation" : true});
        }
        {
            var Q0;
            Q0=makeQuery(id+"F3.opExtrude","CAP_FACE",FACE,{"disambiguationData":[OSD([sQuery(id+"F0.wireOp",EDGE,"E3")])],"isStart":false});
            var sketch = newSketch(context, id + "F18", { "sketchPlane" : qUnion([Q0])});
            skLineSegment(sketch, "E8.bottom", {"start": v(186.83, 27.75) * mm, "end": v(161.83, 27.75) * mm});
            skLineSegment(sketch, "E8.top", {"start": v(186.83, 2.75) * mm, "end": v(161.83, 2.75) * mm});
            skLineSegment(sketch, "E8.left", {"start": v(186.83, 27.75) * mm, "end": v(186.83, 2.75) * mm});
            skLineSegment(sketch, "E8.right", {"start": v(161.83, 27.75) * mm, "end": v(161.83, 2.75) * mm});
            skPoint(sketch, "E8.middle", {"position": v(174.33, 15.25) * mm});
            skSolve(sketch);
        }
        {
            var Q0;
            Q0=makeQuery(id+"F18.imprint","IMPRINT",FACE,{"disambiguationData":[TD([[makeQuery(id+"F18.imprint","IMPRINT",EDGE,{"derivedFrom":sQuery(id+"F18.wireOp",EDGE,"E8.bottom")}),1.0]])]});
            extrude(context, id + "F19", {"entities" : qUnion([Q0]), "operationType" : NewBodyOperationType.REMOVE, "endBound" : BoundingType.THROUGH_ALL, "oppositeDirection" : true, "depth" : 25 * mm, "offsetDistance" : 25 * mm});
        }
        {
            var Q0;
            Q0=makeQuery(id+"F19.boolean.opBoolean","COPY",EDGE,{"derivedFrom":makeQuery(id+"F19.opExtrude","CAP_EDGE",EDGE,{"disambiguationData":[OSD([sQuery(id+"F18.wireOp",EDGE,"E8.bottom")])],"isStart":true})});
            var Q1;
            Q1=makeQuery(id+"F19.boolean.opBoolean","COPY",EDGE,{"derivedFrom":makeQuery(id+"F19.opExtrude","CAP_EDGE",EDGE,{"disambiguationData":[OSD([sQuery(id+"F18.wireOp",EDGE,"E8.left")])],"isStart":true})});
            var Q2;
            Q2=makeQuery(id+"F19.boolean.opBoolean","COPY",EDGE,{"derivedFrom":makeQuery(id+"F19.opExtrude","CAP_EDGE",EDGE,{"disambiguationData":[OSD([sQuery(id+"F18.wireOp",EDGE,"E8.top")])],"isStart":true})});
            var Q3;
            Q3=makeQuery(id+"F19.boolean.opBoolean","COPY",EDGE,{"derivedFrom":makeQuery(id+"F19.opExtrude","CAP_EDGE",EDGE,{"disambiguationData":[OSD([sQuery(id+"F18.wireOp",EDGE,"E8.right")])],"isStart":true})});
            var Q4;
            Q4=makeQuery(id+"F19.boolean.opBoolean","INTERSECT",EDGE,{"derivedFrom":[makeQuery(id+"F3.opExtrude","CAP_FACE",FACE,{"disambiguationData":[OSD([sQuery(id+"F0.wireOp",EDGE,"E3")])],"isStart":true}),makeQuery(id+"F19.opExtrude","SWEPT_FACE",FACE,{"disambiguationData":[OSD([sQuery(id+"F18.wireOp",EDGE,"E8.right")])]})]});
            var Q5;
            Q5=makeQuery(id+"F19.boolean.opBoolean","INTERSECT",EDGE,{"derivedFrom":[makeQuery(id+"F3.opExtrude","CAP_FACE",FACE,{"disambiguationData":[OSD([sQuery(id+"F0.wireOp",EDGE,"E3")])],"isStart":true}),makeQuery(id+"F19.opExtrude","SWEPT_FACE",FACE,{"disambiguationData":[OSD([sQuery(id+"F18.wireOp",EDGE,"E8.bottom")])]})]});
            var Q6;
            Q6=makeQuery(id+"F19.boolean.opBoolean","INTERSECT",EDGE,{"derivedFrom":[makeQuery(id+"F3.opExtrude","CAP_FACE",FACE,{"disambiguationData":[OSD([sQuery(id+"F0.wireOp",EDGE,"E3")])],"isStart":true}),makeQuery(id+"F19.opExtrude","SWEPT_FACE",FACE,{"disambiguationData":[OSD([sQuery(id+"F18.wireOp",EDGE,"E8.left")])]})]});
            var Q7;
            Q7=makeQuery(id+"F19.boolean.opBoolean","INTERSECT",EDGE,{"derivedFrom":[makeQuery(id+"F3.opExtrude","CAP_FACE",FACE,{"disambiguationData":[OSD([sQuery(id+"F0.wireOp",EDGE,"E3")])],"isStart":true}),makeQuery(id+"F19.opExtrude","SWEPT_FACE",FACE,{"disambiguationData":[OSD([sQuery(id+"F18.wireOp",EDGE,"E8.top")])]})]});
            chamfer(context, id + "F20", {"entities" : qUnion([Q0, Q1, Q2, Q3, Q4, Q5, Q6, Q7]), "width" : 0.5 * mm, "tangentPropagation" : true});
        }
    });
